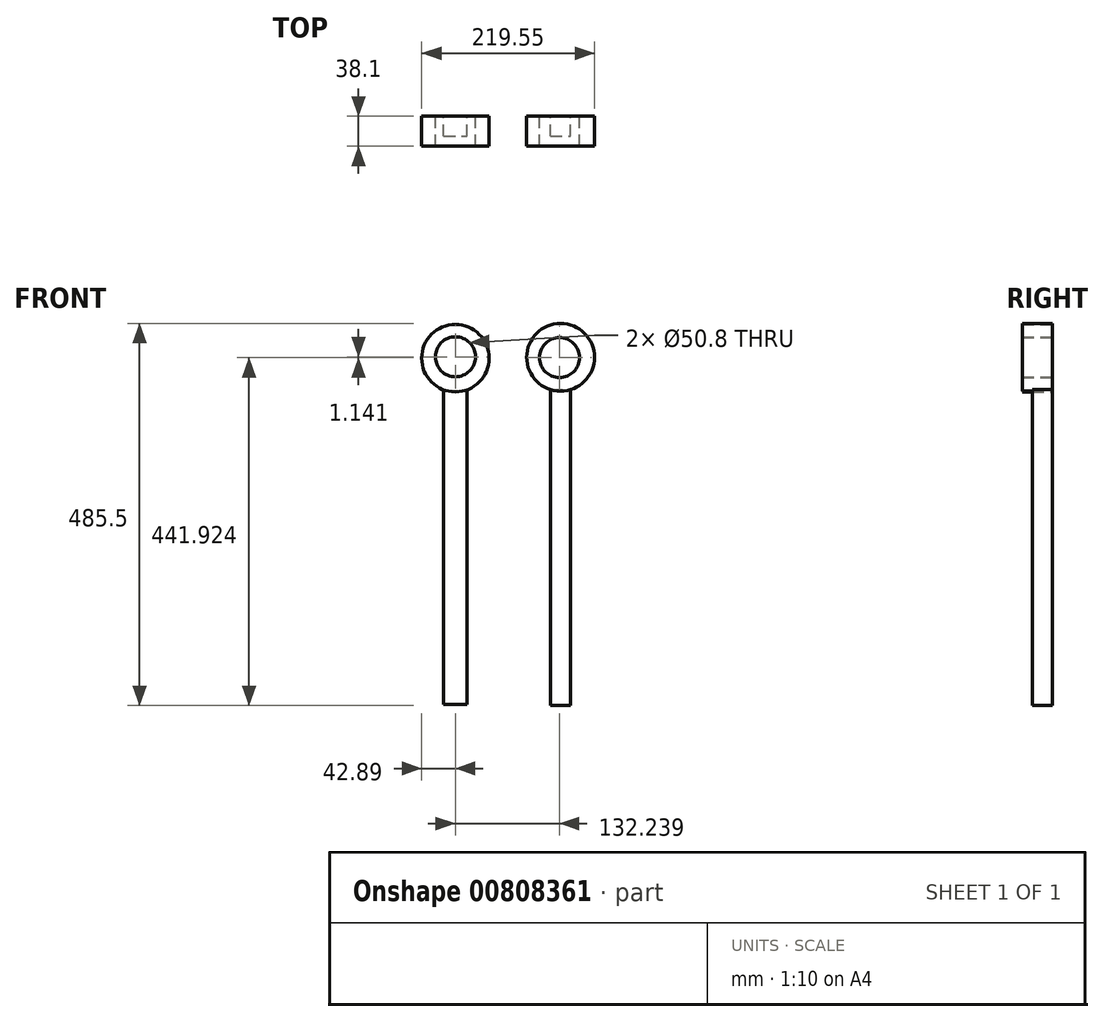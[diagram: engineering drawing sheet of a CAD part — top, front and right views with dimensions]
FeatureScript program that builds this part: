
annotation { "Feature Type Name" : "Feature", "Feature Type Description" : "" }
export const myFeature = defineFeature(function(context is Context, id is Id, definition is map)
    precondition{}
    {
        {
            var Q0;
            Q0=qCreatedBy(makeId("Front.planeOp"),FACE);
            var sketch = newSketch(context, id + "F0", { "sketchPlane" : qUnion([Q0])});
            skLineSegment(sketch, "E0.bottom", {"start": v(-14.98, -199.44) * mm, "end": v(14.98, -199.44) * mm});
            skLineSegment(sketch, "E0.top", {"start": v(-14.98, 199.44) * mm, "end": v(14.98, 199.44) * mm});
            skLineSegment(sketch, "E0.left", {"start": v(-14.98, -199.44) * mm, "end": v(-14.98, 199.44) * mm});
            skLineSegment(sketch, "E0.right", {"start": v(14.98, -199.44) * mm, "end": v(14.98, 199.44) * mm});
            skPoint(sketch, "E0.middle", {"position": v(0, 0) * mm});
            skLineSegment(sketch, "E1.bottom", {"start": v(120.54, -200.6) * mm, "end": v(146.02, -200.6) * mm});
            skLineSegment(sketch, "E1.top", {"start": v(120.54, 200.6) * mm, "end": v(146.02, 200.6) * mm});
            skLineSegment(sketch, "E1.left", {"start": v(120.54, -200.6) * mm, "end": v(120.54, 200.6) * mm});
            skLineSegment(sketch, "E1.right", {"start": v(146.02, -200.6) * mm, "end": v(146.02, 200.6) * mm});
            skPoint(sketch, "E1.middle", {"position": v(133.28, 0) * mm});
            skSolve(sketch);
        }
        {
            var Q0;
            Q0=makeQuery(id+"F0.imprint","IMPRINT",FACE,{"disambiguationData":[TD([[makeQuery(id+"F0.imprint","IMPRINT",EDGE,{"derivedFrom":sQuery(id+"F0.wireOp",EDGE,"E0.bottom")}),1.0]])]});
            var Q1;
            Q1=makeQuery(id+"F0.imprint","IMPRINT",FACE,{"disambiguationData":[TD([[makeQuery(id+"F0.imprint","IMPRINT",EDGE,{"derivedFrom":sQuery(id+"F0.wireOp",EDGE,"E1.bottom")}),1.0]])]});
            extrude(context, id + "F1", {"entities" : qUnion([Q0, Q1]), "depth" : 25.4 * mm, "offsetDistance" : 25.4 * mm});
        }
        {
            var Q0;
            Q0=qCreatedBy(makeId("Front.planeOp"),FACE);
            var sketch = newSketch(context, id + "F2", { "sketchPlane" : qUnion([Q0])});
            skCircle(sketch, "E2", {"center": v(0, 240.7) * mm, "radius": 42.9 * mm});
            skCircle(sketch, "E3", {"center": v(133.62, 241.86) * mm, "radius": 43.04 * mm});
            skSolve(sketch);
        }
        {
            var Q0;
            Q0=makeQuery(id+"F2.imprint","IMPRINT",FACE,{"disambiguationData":[TD([[makeQuery(id+"F2.imprint","IMPRINT",EDGE,{"derivedFrom":sQuery(id+"F2.wireOp",EDGE,"E3")}),1.0]])]});
            var Q1;
            Q1=makeQuery(id+"F2.imprint","IMPRINT",FACE,{"disambiguationData":[TD([[makeQuery(id+"F2.imprint","IMPRINT",EDGE,{"derivedFrom":sQuery(id+"F2.wireOp",EDGE,"E2")}),1.0]])]});
            extrude(context, id + "F3", {"entities" : qUnion([Q0, Q1]), "depth" : 38.1 * mm, "offsetDistance" : 25.4 * mm});
        }
        {
            var Q0;
            Q0=qCreatedBy(makeId("Front.planeOp"),FACE);
            var sketch = newSketch(context, id + "F4", { "sketchPlane" : qUnion([Q0])});
            skCircle(sketch, "E4", {"center": v(0, 242.47) * mm, "radius": 25.4 * mm});
            skCircle(sketch, "E5", {"center": v(132.24, 241.32) * mm, "radius": 25.4 * mm});
            skSolve(sketch);
        }
        {
            var Q0;
            Q0=sQuery(id+"F4.wireOp",VERTEX,"E4.center");
            var Q1;
            Q1=sQuery(id+"F4.wireOp",VERTEX,"E5.center");
            var Q2;
            Q2=makeQuery(id+"F3.opExtrude","SWEPT_BODY",BODY,{"disambiguationData":[OSD([sQuery(id+"F2.wireOp",EDGE,"E2")])]});
            var Q3;
            Q3=makeQuery(id+"F3.opExtrude","SWEPT_BODY",BODY,{"disambiguationData":[OSD([sQuery(id+"F2.wireOp",EDGE,"E3")])]});
            hole(context, id + "F5", {"style" : HoleStyle.SIMPLE, "endStyle" : HoleEndStyle.THROUGH, "oppositeDirection" : true, "holeDiameter" : 50.8 * mm, "majorDiameter" : 6.35 * mm, "isTappedThrough" : true, "tappedDepth" : 12.7 * mm, "tapClearance" : 3, "locations" : qUnion([Q0, Q1]), "scope" : qUnion([Q2, Q3])});
        }
    });
